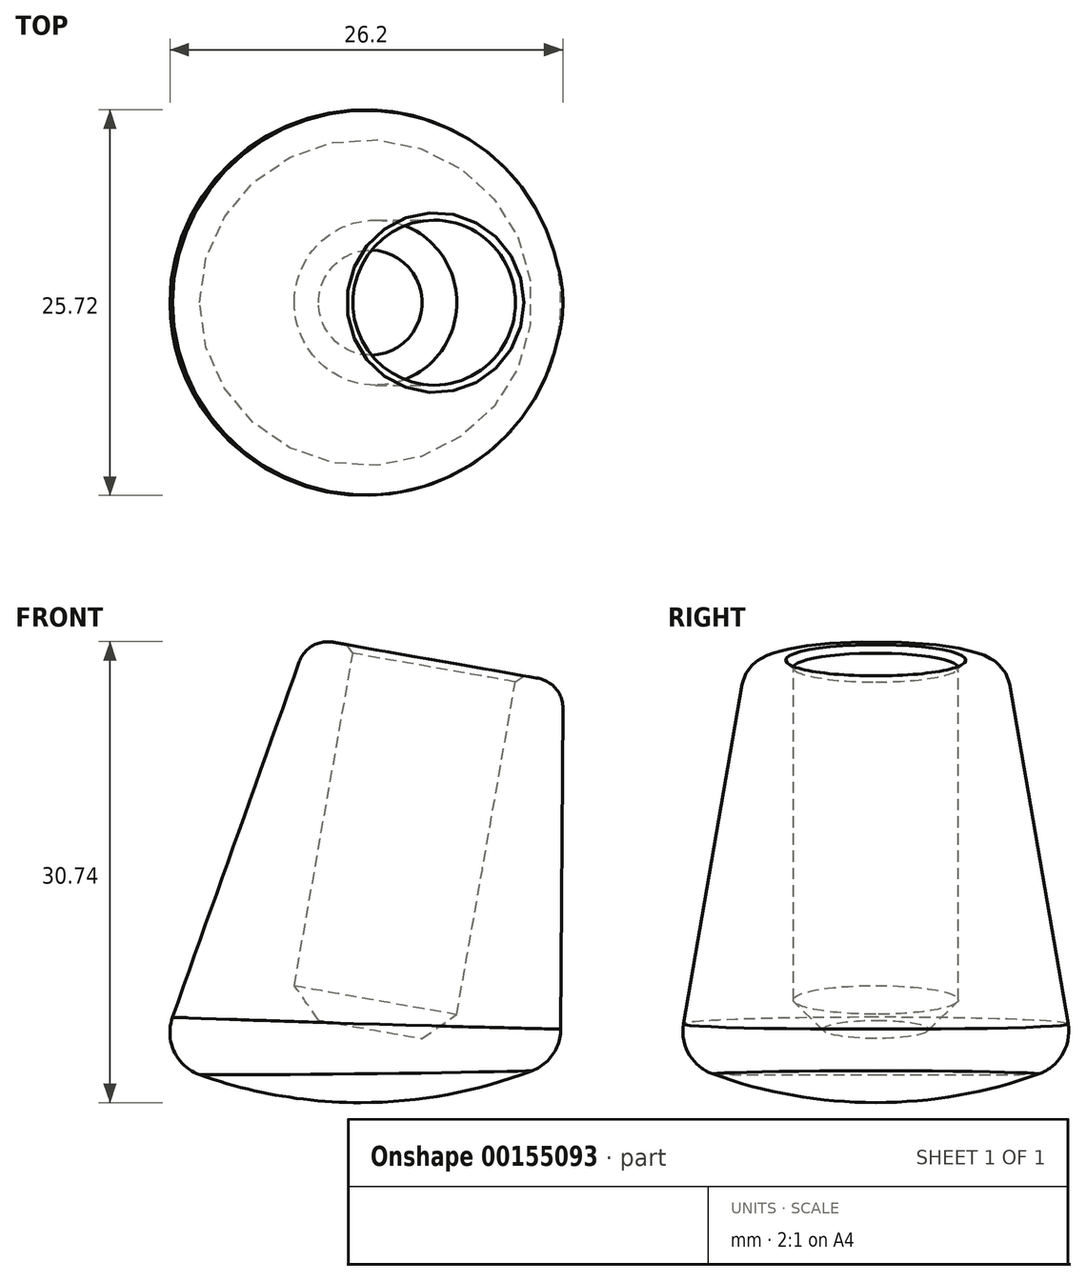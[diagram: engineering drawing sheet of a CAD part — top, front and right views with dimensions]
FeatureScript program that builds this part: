
annotation { "Feature Type Name" : "Feature", "Feature Type Description" : "" }
export const myFeature = defineFeature(function(context is Context, id is Id, definition is map)
    precondition{}
    {
        {
            var Q0;
            Q0=qCreatedBy(makeId("Front.planeOp"),FACE);
            var sketch = newSketch(context, id + "F0", { "sketchPlane" : qUnion([Q0])});
            skLineSegment(sketch, "E0", {"start": v(0, 0) * mm, "end": v(0, 25) * mm});
            skLineSegment(sketch, "E1", {"start": v(0, 25) * mm, "end": v(-17.01, 28) * mm});
            skLineSegment(sketch, "E2", {"start": v(-17.01, 28) * mm, "end": v(-27, 0) * mm});
            skLineSegment(sketch, "E3", {"start": v(-27, 0) * mm, "end": v(0, 0) * mm});
            skArc(sketch, "E4", {"start": v(-27, 0) * mm, "mid": v(-13.5, -3) * mm, "end": v(0, 0) * mm});
            skPoint(sketch, "E5", {"position": v(-13.5, -3) * mm});
            skPoint(sketch, "E6", {"position": v(-8.5, 26.5) * mm});
            skCircle(sketch, "E7", {"center": v(-8.5, 26.5) * mm, "radius": 5.5 * mm, "construction": true});
            skPoint(sketch, "E8", {"position": v(-13.92, 27.46) * mm});
            skPoint(sketch, "E9", {"position": v(-3.1, 25.54) * mm});
            skLineSegment(sketch, "E10", {"start": v(-13.92, 27.46) * mm, "end": v(-18.26, 2.83) * mm});
            skLineSegment(sketch, "E11", {"start": v(-18.26, 2.83) * mm, "end": v(-7.43, 0.92) * mm});
            skLineSegment(sketch, "E12", {"start": v(-7.43, 0.92) * mm, "end": v(-3.1, 25.54) * mm});
            skLineSegment(sketch, "E13", {"start": v(-8.5, 26.5) * mm, "end": v(-17.54, -24.7) * mm});
            skLineSegment(sketch, "E14", {"start": v(-8.5, 26.5) * mm, "end": v(0, 74.75) * mm, "construction": true});
            skLineSegment(sketch, "E15", {"start": v(0, 74.75) * mm, "end": v(0, 25) * mm, "construction": true});
            skLineSegment(sketch, "E16", {"start": v(-13.5, -3) * mm, "end": v(-13.5, 0) * mm});
            skSolve(sketch);
        }
        {
            var Q0;
            {var subQ2=sQuery(id+"F0.wireOp",EDGE,"E2");Q0=makeQuery(id+"F0.imprint","IMPRINT",FACE,{"disambiguationData":[TD([[makeQuery(id+"F0.imprint","IMPRINT",EDGE,{"derivedFrom":subQ2}),1.0]])]});}
            var Q1;
            Q1=sQuery(id+"F0.wireOp",EDGE,"E13");
            revolve(context, id + "F1", {"entities" : qUnion([Q0]), "axis" : qUnion([Q1]), "revolveType" : RevolveType.FULL});
        }
        {
            var Q0;
            Q0=qCreatedBy(makeId("Top.planeOp"),FACE);
            var sketch = newSketch(context, id + "F2", { "sketchPlane" : qUnion([Q0])});
            skLineSegment(sketch, "E17.bottom", {"start": v(23.86, 39.6) * mm, "end": v(-55.33, 39.6) * mm});
            skLineSegment(sketch, "E17.top", {"start": v(23.86, -39.6) * mm, "end": v(-55.33, -39.6) * mm});
            skLineSegment(sketch, "E17.left", {"start": v(23.86, 39.6) * mm, "end": v(23.86, -39.6) * mm});
            skLineSegment(sketch, "E17.right", {"start": v(-55.33, 39.6) * mm, "end": v(-55.33, -39.6) * mm});
            skPoint(sketch, "E17.middle", {"position": v(-15.73, 0) * mm});
            skSolve(sketch);
        }
        {
            var Q0;
            Q0=makeQuery(id+"F2.imprint","IMPRINT",FACE,{"disambiguationData":[TD([[makeQuery(id+"F2.imprint","IMPRINT",EDGE,{"derivedFrom":sQuery(id+"F2.wireOp",EDGE,"E17.bottom")}),1.0]])]});
            extrude(context, id + "F3", {"entities" : qUnion([Q0]), "operationType" : NewBodyOperationType.REMOVE, "oppositeDirection" : true, "depth" : 25 * mm});
        }
        {
            var Q0;
            {var subQ0=sQuery(id+"F0.wireOp",EDGE,"E16");var subQ1=sQuery(id+"F0.wireOp",EDGE,"E4");var subQ2=makeQuery(id+"F0.imprint","INTERSECT",VERTEX,{"derivedFrom":[subQ1,subQ0]});Q0=makeQuery(id+"F0.imprint","IMPRINT",FACE,{"disambiguationData":[TD([[makeQuery(id+"F0.imprint","IMPRINT",EDGE,{"disambiguationData":[TD([[subQ2,1.0]])],"derivedFrom":subQ1}),1.0]])]});}
            var Q1;
            {var subQ0=sQuery(id+"F0.wireOp",EDGE,"E4");var subQ5=sQuery(id+"F0.wireOp",EDGE,"E13");var subQ6=makeQuery(id+"F0.imprint","INTERSECT",VERTEX,{"derivedFrom":[subQ0,subQ5]});Q1=makeQuery(id+"F0.imprint","IMPRINT",FACE,{"disambiguationData":[TD([[makeQuery(id+"F0.imprint","IMPRINT",EDGE,{"disambiguationData":[TD([[subQ6,1.0]])],"derivedFrom":subQ5}),-1.0]])]});}
            var Q2;
            Q2=sQuery(id+"F0.wireOp",EDGE,"E16");
            revolve(context, id + "F4", {"operationType" : NewBodyOperationType.ADD, "entities" : qUnion([Q0, Q1]), "axis" : qUnion([Q2]), "revolveType" : RevolveType.FULL});
        }
        {
            var Q0;
            Q0=makeQuery(id+"F4.opRevolve","SWEPT_EDGE",EDGE,{"disambiguationData":[OSD([sQuery(id+"F0.wireOp",EDGE,"E2"),sQuery(id+"F0.wireOp",EDGE,"E3"),sQuery(id+"F0.wireOp",EDGE,"E4")])]});
            fillet(context, id + "F5", {"entities" : qUnion([Q0]), "radius" : 3 * mm, "tangentPropagation" : true, "allowEdgeOverflow" : false});
        }
        {
            var Q0;
            Q0=makeQuery(id+"F1.opRevolve","SWEPT_EDGE",EDGE,{"disambiguationData":[OSD([sQuery(id+"F0.wireOp",EDGE,"E10"),sQuery(id+"F0.wireOp",EDGE,"E11")])]});
            chamfer(context, id + "F6", {"entities" : qUnion([Q0]), "width" : 2 * mm, "tangentPropagation" : true});
        }
        {
            var Q0;
            Q0=makeQuery(id+"F1.opRevolve","SWEPT_EDGE",EDGE,{"disambiguationData":[OSD([sQuery(id+"F0.wireOp",EDGE,"E1"),sQuery(id+"F0.wireOp",EDGE,"E2")])]});
            fillet(context, id + "F7", {"entities" : qUnion([Q0]), "radius" : 2 * mm, "tangentPropagation" : true, "allowEdgeOverflow" : false});
        }
        {
            var Q0;
            Q0=makeQuery(id+"F1.opRevolve","SWEPT_EDGE",EDGE,{"disambiguationData":[OSD([sQuery(id+"F0.wireOp",EDGE,"E1"),sQuery(id+"F0.wireOp",EDGE,"E10")])]});
            chamfer(context, id + "F8", {"entities" : qUnion([Q0]), "width" : 0.5 * mm, "tangentPropagation" : true});
        }
    });
